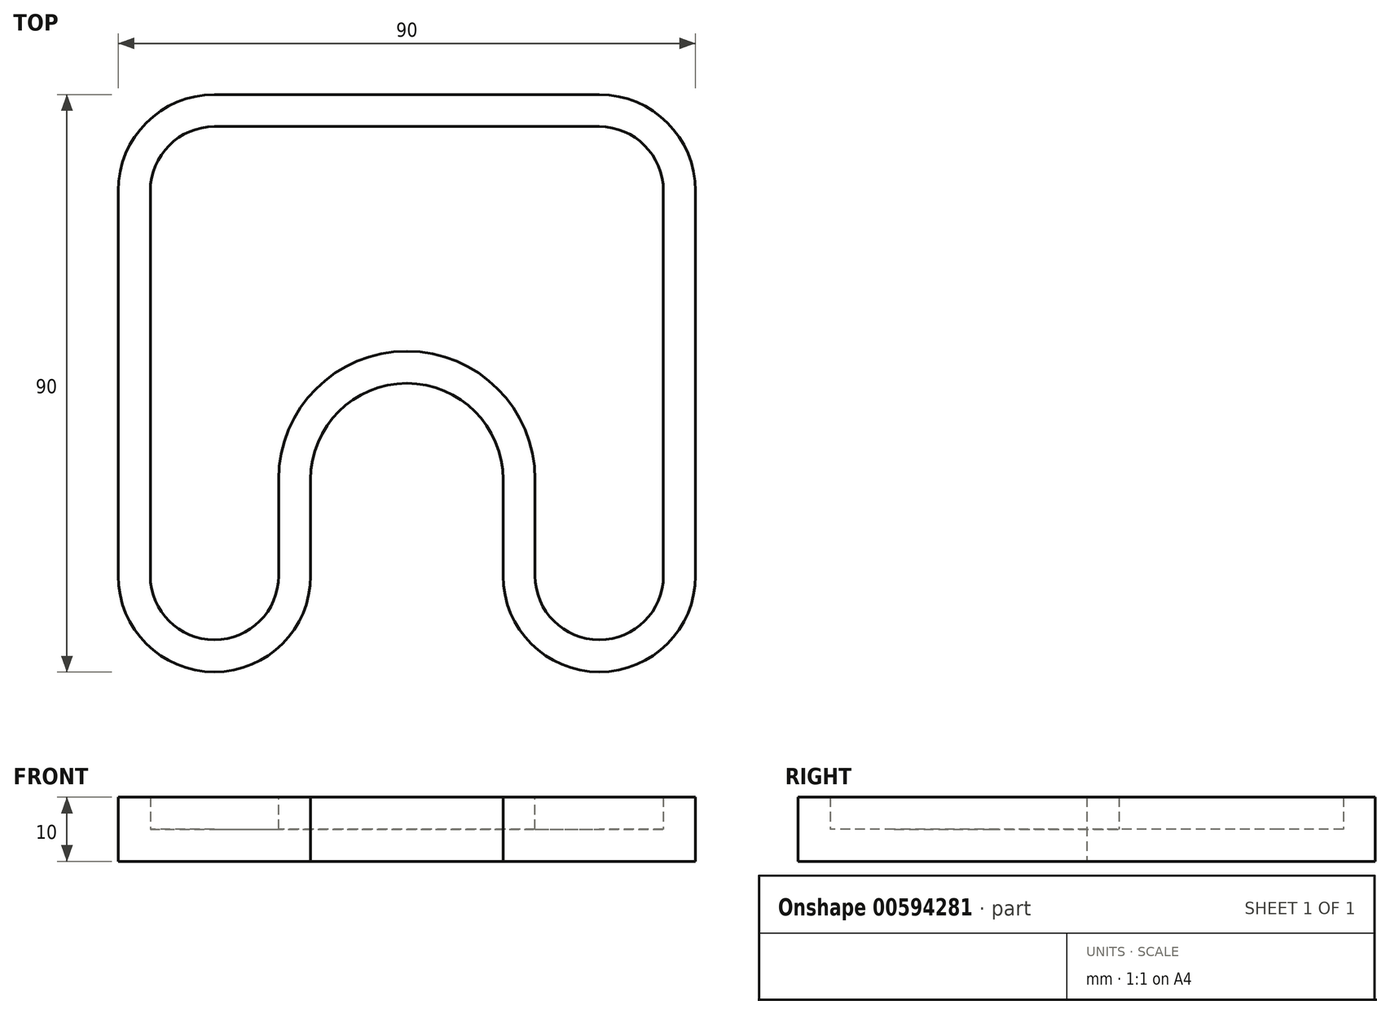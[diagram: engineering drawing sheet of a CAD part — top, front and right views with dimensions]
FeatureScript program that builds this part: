
annotation { "Feature Type Name" : "Feature", "Feature Type Description" : "" }
export const myFeature = defineFeature(function(context is Context, id is Id, definition is map)
    precondition{}
    {
        {
            var Q0;
            Q0=qCreatedBy(makeId("Top.planeOp"),FACE);
            var sketch = newSketch(context, id + "F0", { "sketchPlane" : qUnion([Q0])});
            skLineSegment(sketch, "E0.bottom", {"start": v(-30, 45) * mm, "end": v(30, 45) * mm});
            skLineSegment(sketch, "E0.top", {"start": v(-30, -45) * mm, "end": v(-30, -45) * mm});
            skLineSegment(sketch, "E0.left", {"start": v(-45, 30) * mm, "end": v(-45, -30) * mm});
            skLineSegment(sketch, "E0.right", {"start": v(45, 30) * mm, "end": v(45, -30) * mm});
            skPoint(sketch, "E0.middle", {"position": v(0, 0) * mm});
            skPoint(sketch, "E1.middle", {"position": v(-4.6, 41.05) * mm});
            skLineSegment(sketch, "E2", {"start": v(-15, -30) * mm, "end": v(-15, -15) * mm});
            skLineSegment(sketch, "E3", {"start": v(0, 0) * mm, "end": v(0, 0) * mm});
            skLineSegment(sketch, "E4", {"start": v(15, -30) * mm, "end": v(15, -15) * mm});
            skPoint(sketch, "E5.visualSharp", {"position": v(-45, 45) * mm});
            skArc(sketch, "E5.filletArc", {"start": v(-30, 45) * mm, "mid": v(-40.6, 40.6) * mm, "end": v(-45, 30) * mm});
            skPoint(sketch, "E6.visualSharp", {"position": v(45, 45) * mm});
            skArc(sketch, "E6.filletArc", {"start": v(45, 30) * mm, "mid": v(40.6, 40.6) * mm, "end": v(30, 45) * mm});
            skPoint(sketch, "E7.visualSharp", {"position": v(45, -45) * mm});
            skArc(sketch, "E7.filletArc", {"start": v(30, -45) * mm, "mid": v(40.6, -40.6) * mm, "end": v(45, -30) * mm});
            skPoint(sketch, "E8.visualSharp", {"position": v(-45, -45) * mm});
            skArc(sketch, "E8.filletArc", {"start": v(-45, -30) * mm, "mid": v(-40.6, -40.6) * mm, "end": v(-30, -45) * mm});
            skPoint(sketch, "E9.visualSharp", {"position": v(-15, 0) * mm});
            skArc(sketch, "E9.filletArc", {"start": v(0, 0) * mm, "mid": v(-10.6, -4.4) * mm, "end": v(-15, -15) * mm});
            skPoint(sketch, "E10.visualSharp", {"position": v(15, 0) * mm});
            skArc(sketch, "E10.filletArc", {"start": v(15, -15) * mm, "mid": v(10.6, -4.4) * mm, "end": v(0, 0) * mm});
            skArc(sketch, "E11.filletArc", {"start": v(-30, -45) * mm, "mid": v(-19.4, -40.6) * mm, "end": v(-15, -30) * mm});
            skLineSegment(sketch, "E12", {"start": v(30, -45) * mm, "end": v(30, -45) * mm});
            skPoint(sketch, "E13.visualSharp", {"position": v(15, -45) * mm});
            skArc(sketch, "E13.filletArc", {"start": v(15, -30) * mm, "mid": v(19.4, -40.6) * mm, "end": v(30, -45) * mm});
            skSolve(sketch);
        }
        {
            var Q0;
            Q0=makeQuery(id+"F0.imprint","IMPRINT",FACE,{"disambiguationData":[TD([[makeQuery(id+"F0.imprint","IMPRINT",EDGE,{"derivedFrom":sQuery(id+"F0.wireOp",EDGE,"E0.bottom")}),-1.0]])]});
            extrude(context, id + "F1", {"entities" : qUnion([Q0]), "depth" : 10 * mm, "offsetDistance" : 25 * mm});
        }
        {
            var Q0;
            Q0=makeQuery(id+"F1.opExtrude","CAP_FACE",FACE,{"disambiguationData":[OSD([sQuery(id+"F0.wireOp",EDGE,"E0.bottom"),sQuery(id+"F0.wireOp",EDGE,"E0.left"),sQuery(id+"F0.wireOp",EDGE,"E0.right"),sQuery(id+"F0.wireOp",EDGE,"E2"),sQuery(id+"F0.wireOp",EDGE,"E4"),sQuery(id+"F0.wireOp",EDGE,"E5.filletArc"),sQuery(id+"F0.wireOp",EDGE,"E6.filletArc"),sQuery(id+"F0.wireOp",EDGE,"E7.filletArc"),sQuery(id+"F0.wireOp",EDGE,"E8.filletArc"),sQuery(id+"F0.wireOp",EDGE,"E9.filletArc"),sQuery(id+"F0.wireOp",EDGE,"E10.filletArc"),sQuery(id+"F0.wireOp",EDGE,"E11.filletArc"),sQuery(id+"F0.wireOp",EDGE,"E13.filletArc")])],"isStart":false});
            shell(context, id + "F2", {"entities" : qUnion([Q0]), "thickness" : 5 * mm});
        }
    });
